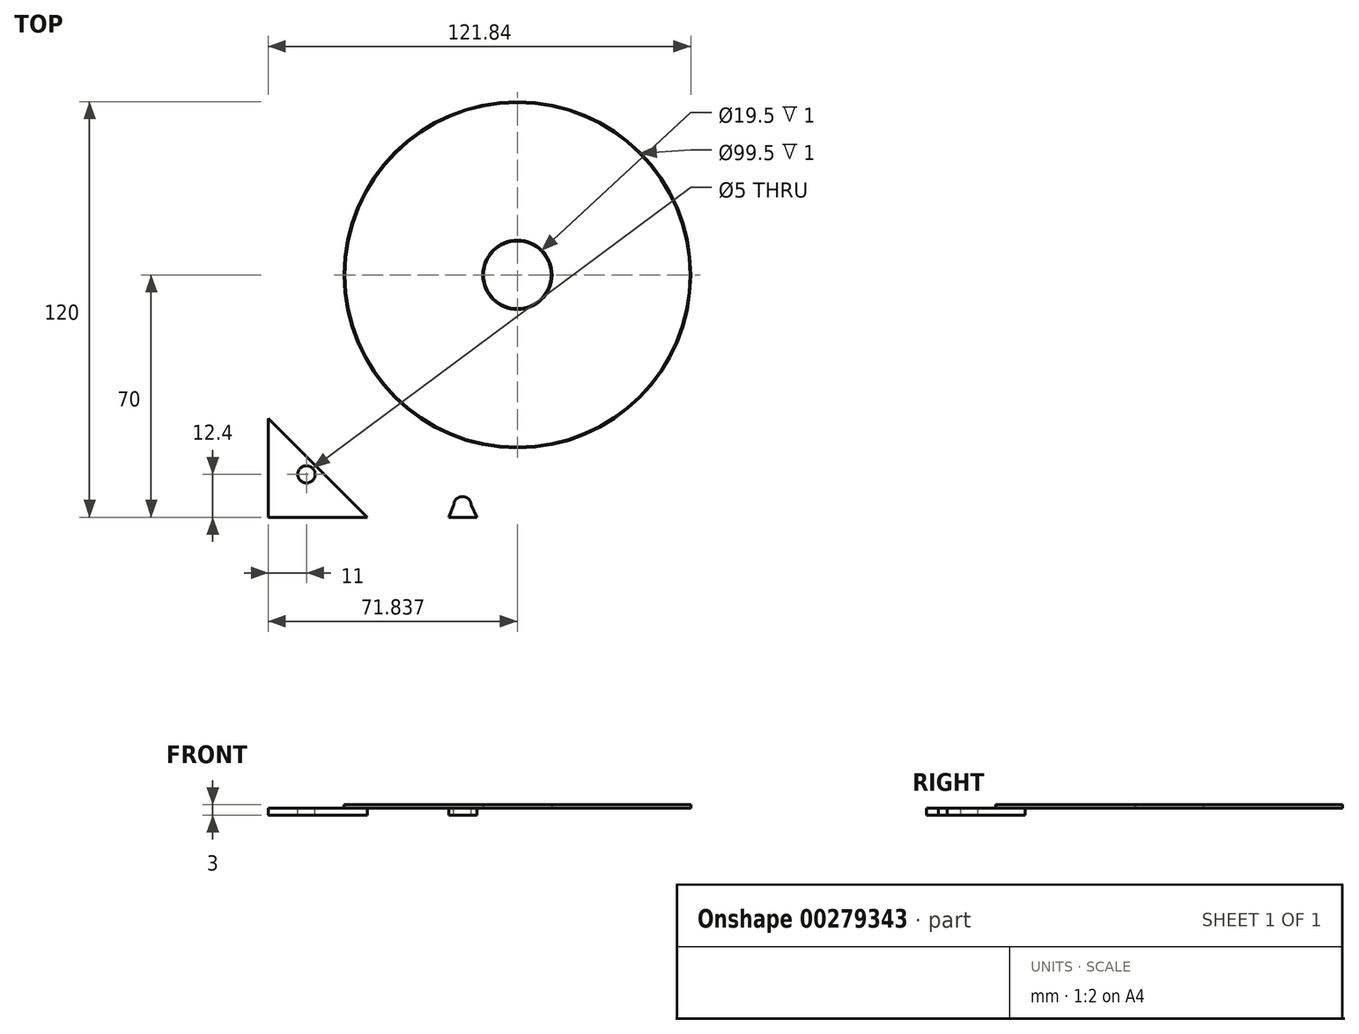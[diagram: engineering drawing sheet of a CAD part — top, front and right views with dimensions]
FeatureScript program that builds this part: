
annotation { "Feature Type Name" : "Feature", "Feature Type Description" : "" }
export const myFeature = defineFeature(function(context is Context, id is Id, definition is map)
    precondition{}
    {
        {
            var Q0;
            Q0=qCreatedBy(makeId("Top.planeOp"),FACE);
            var sketch = newSketch(context, id + "F0", { "sketchPlane" : qUnion([Q0])});
            skLineSegment(sketch, "E0.bottom", {"start": v(75, 70) * mm, "end": v(-75, 70) * mm});
            skLineSegment(sketch, "E0.top", {"start": v(75, -70) * mm, "end": v(-75, -70) * mm});
            skLineSegment(sketch, "E0.left", {"start": v(75, 70) * mm, "end": v(75, -70) * mm});
            skLineSegment(sketch, "E0.right", {"start": v(-75, 70) * mm, "end": v(-75, -70) * mm});
            skPoint(sketch, "E0.middle", {"position": v(0, 0) * mm});
            skSolve(sketch);
        }
        {
            var Q0;
            Q0=qSketchRegion(id+"F0",true);
            extrude(context, id + "F1", {"entities" : qUnion([Q0]), "depth" : 2 * mm});
        }
        {
            var Q0;
            Q0=makeQuery(id+"F1.opExtrude","CAP_FACE",FACE,{"disambiguationData":[OSD([sQuery(id+"F0.wireOp",EDGE,"E0.bottom"),sQuery(id+"F0.wireOp",EDGE,"E0.top"),sQuery(id+"F0.wireOp",EDGE,"E0.left"),sQuery(id+"F0.wireOp",EDGE,"E0.right")])],"isStart":false});
            var sketch = newSketch(context, id + "F2", { "sketchPlane" : qUnion([Q0])});
            skArc(sketch, "E1", {"start": v(-67.18, 6.35) * mm, "mid": v(-67.92, 8.12) * mm, "end": v(-69.68, 8.85) * mm});
            skArc(sketch, "E2.MirrorC", {"start": v(-67.18, -6.35) * mm, "mid": v(-67.92, -8.12) * mm, "end": v(-69.68, -8.85) * mm});
            skArc(sketch, "E3", {"start": v(-21.5, 66.52) * mm, "mid": v(-19, 64) * mm, "end": v(-16.5, 66.52) * mm});
            skCircle(sketch, "E4", {"center": v(-64, 57.6) * mm, "radius": 2.5 * mm});
            skArc(sketch, "E5.MirrorC", {"start": v(-21.5, -66.52) * mm, "mid": v(-19, -64) * mm, "end": v(-16.5, -66.52) * mm});
            skCircle(sketch, "E6.MirrorC", {"center": v(-64, -57.6) * mm, "radius": 2.5 * mm});
            skLineSegment(sketch, "E7", {"start": v(-21.5, 66.52) * mm, "end": v(-22.94, 70) * mm});
            skLineSegment(sketch, "E8.MirrorCS", {"start": v(-16.5, 66.52) * mm, "end": v(-14.88, 70) * mm});
            skLineSegment(sketch, "E9.MirrorCS", {"start": v(-16.5, -66.52) * mm, "end": v(-14.88, -70) * mm});
            skLineSegment(sketch, "E10.MirrorCS", {"start": v(-21.5, -66.52) * mm, "end": v(-22.94, -70) * mm});
            skLineSegment(sketch, "E11", {"start": v(-46.5, 70) * mm, "end": v(-75, 41.5) * mm});
            skLineSegment(sketch, "E12.MirrorCS", {"start": v(-46.5, -70) * mm, "end": v(-75, -41.5) * mm});
            skLineSegment(sketch, "E13", {"start": v(-69.68, 8.85) * mm, "end": v(-75, 8.85) * mm});
            skLineSegment(sketch, "E14", {"start": v(-67.18, -6.35) * mm, "end": v(-67.18, 6.35) * mm});
            skLineSegment(sketch, "E15.MirrorCS", {"start": v(-69.68, -8.85) * mm, "end": v(-75, -8.85) * mm});
            skSolve(sketch);
        }
        {
            var Q0;
            Q0=qSketchRegion(id+"F2",true);
            var Q1;
            Q1=makeQuery(id+"F2.imprint","IMPRINT",FACE,{"disambiguationData":[TD([[makeQuery(id+"F2.imprint","IMPRINT",EDGE,{"derivedFrom":sQuery(id+"F2.wireOp",EDGE,"E4")}),-1.0]])]});
            var Q2;
            Q2=makeQuery(id+"F2.imprint","IMPRINT",FACE,{"disambiguationData":[TD([[makeQuery(id+"F2.imprint","IMPRINT",EDGE,{"derivedFrom":sQuery(id+"F2.wireOp",EDGE,"E1")}),1.0]])]});
            var Q3;
            Q3=makeQuery(id+"F2.imprint","IMPRINT",FACE,{"disambiguationData":[TD([[makeQuery(id+"F2.imprint","IMPRINT",EDGE,{"derivedFrom":sQuery(id+"F2.wireOp",EDGE,"E5.MirrorC")}),-1.0]])]});
            var Q4;
            Q4=makeQuery(id+"F2.imprint","IMPRINT",FACE,{"disambiguationData":[TD([[makeQuery(id+"F2.imprint","IMPRINT",EDGE,{"derivedFrom":sQuery(id+"F2.wireOp",EDGE,"E3")}),1.0]])]});
            var Q5;
            Q5=makeQuery(id+"F2.imprint","IMPRINT",FACE,{"disambiguationData":[TD([[makeQuery(id+"F2.imprint","IMPRINT",EDGE,{"derivedFrom":sQuery(id+"F2.wireOp",EDGE,"E6.MirrorC")}),1.0]])]});
            extrude(context, id + "F3", {"entities" : qUnion([Q0, Q1, Q2, Q3, Q4, Q5]), "operationType" : NewBodyOperationType.REMOVE, "oppositeDirection" : true, "depth" : 5 * mm});
        }
        {
            var Q0;
            Q0=makeQuery(id+"F1.opExtrude","CAP_FACE",FACE,{"disambiguationData":[OSD([sQuery(id+"F0.wireOp",EDGE,"E0.bottom"),sQuery(id+"F0.wireOp",EDGE,"E0.top"),sQuery(id+"F0.wireOp",EDGE,"E0.left"),sQuery(id+"F0.wireOp",EDGE,"E0.right")])],"isStart":false});
            var sketch = newSketch(context, id + "F4", { "sketchPlane" : qUnion([Q0])});
            skCircle(sketch, "E16", {"center": v(-3.16, 0) * mm, "radius": 49.75 * mm});
            skCircle(sketch, "E17", {"center": v(-3.16, 0) * mm, "radius": 50 * mm});
            skSolve(sketch);
        }
        {
            var Q0;
            Q0=makeQuery(id+"F4.imprint","IMPRINT",FACE,{"disambiguationData":[TD([[makeQuery(id+"F4.imprint","IMPRINT",EDGE,{"derivedFrom":sQuery(id+"F4.wireOp",EDGE,"E16")}),-1.0]])]});
            extrude(context, id + "F5", {"entities" : qUnion([Q0]), "operationType" : NewBodyOperationType.ADD, "depth" : 1 * mm});
        }
        {
            var Q0;
            Q0=makeQuery(id+"F5.boolean.opBoolean","SPLIT",FACE,{"disambiguationData":[TD([makeQuery(id+"F5.opExtrude","SWEPT_FACE",FACE,{"disambiguationData":[OSD([sQuery(id+"F4.wireOp",EDGE,"E16")])]})])],"derivedFrom":makeQuery(id+"F1.opExtrude","CAP_FACE",FACE,{"disambiguationData":[OSD([sQuery(id+"F0.wireOp",EDGE,"E0.bottom"),sQuery(id+"F0.wireOp",EDGE,"E0.top"),sQuery(id+"F0.wireOp",EDGE,"E0.left"),sQuery(id+"F0.wireOp",EDGE,"E0.right")])],"isStart":false})});
            var sketch = newSketch(context, id + "F6", { "sketchPlane" : qUnion([Q0])});
            skCircle(sketch, "E18", {"center": v(-3.16, 0) * mm, "radius": 9.75 * mm});
            skCircle(sketch, "E19", {"center": v(-3.16, 0) * mm, "radius": 10 * mm});
            skSolve(sketch);
        }
        {
            var Q0;
            Q0=makeQuery(id+"F6.imprint","IMPRINT",FACE,{"disambiguationData":[TD([[makeQuery(id+"F6.imprint","IMPRINT",EDGE,{"derivedFrom":sQuery(id+"F6.wireOp",EDGE,"E18")}),-1.0]])]});
            extrude(context, id + "F7", {"entities" : qUnion([Q0]), "operationType" : NewBodyOperationType.ADD, "depth" : 1 * mm});
        }
    });
